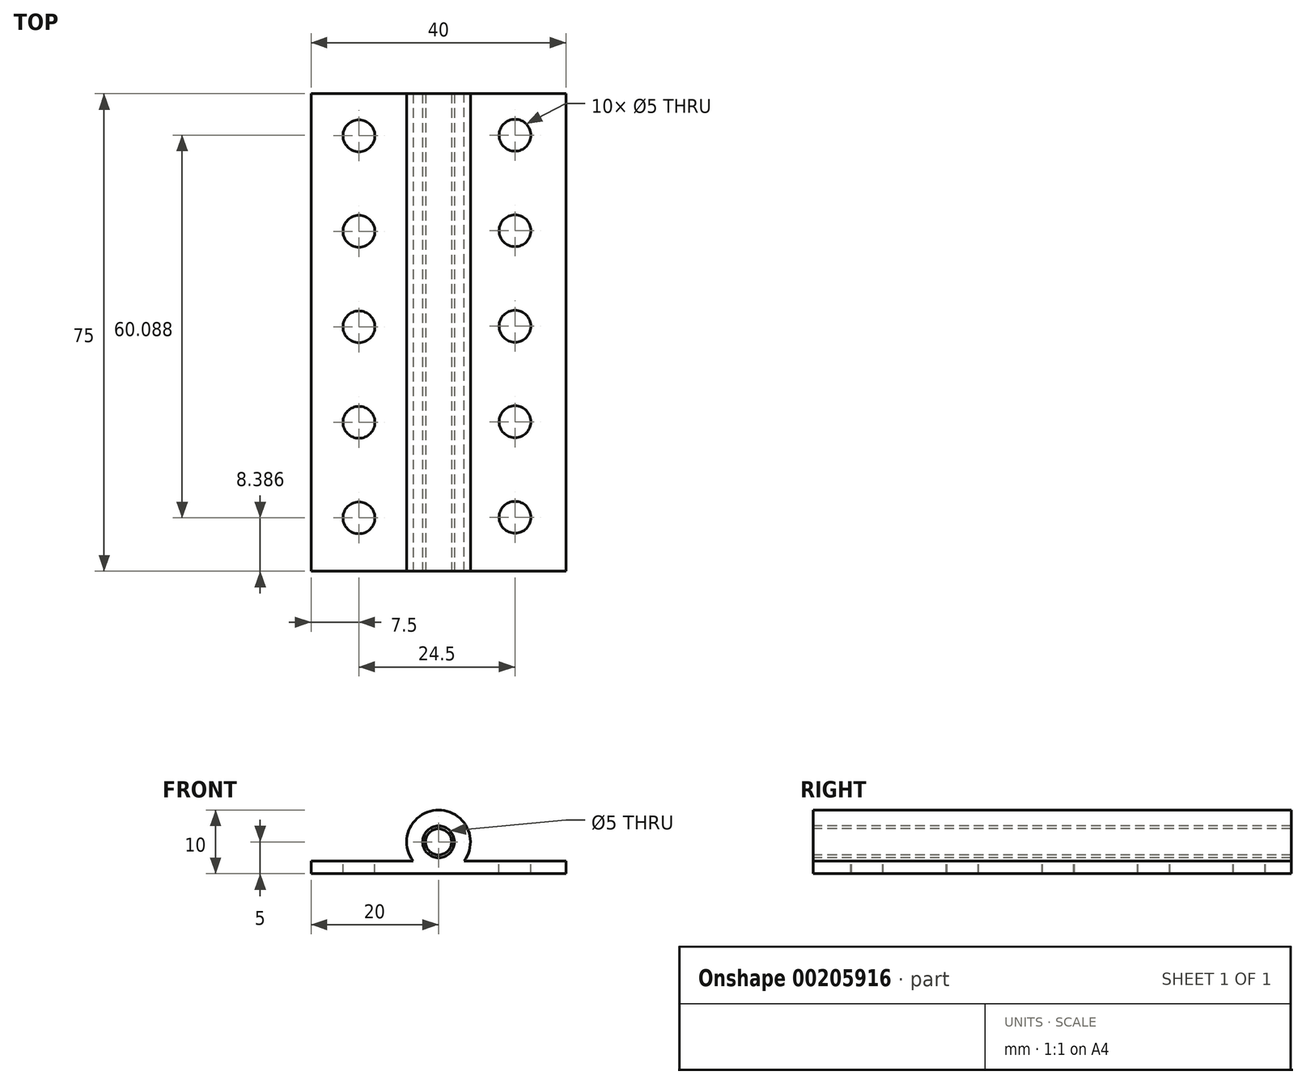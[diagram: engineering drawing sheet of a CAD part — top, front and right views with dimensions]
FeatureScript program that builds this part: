
annotation { "Feature Type Name" : "Feature", "Feature Type Description" : "" }
export const myFeature = defineFeature(function(context is Context, id is Id, definition is map)
    precondition{}
    {
        {
            var Q0;
            Q0=qCreatedBy(makeId("Front.planeOp"),FACE);
            var sketch = newSketch(context, id + "F0", { "sketchPlane" : qUnion([Q0])});
            skCircle(sketch, "E0", {"center": v(0, 0) * mm, "radius": 5 * mm});
            skSolve(sketch);
        }
        {
            var Q0;
            Q0=qCreatedBy(makeId("Front.planeOp"),FACE);
            var sketch = newSketch(context, id + "F1", { "sketchPlane" : qUnion([Q0])});
            skLineSegment(sketch, "E1.bottom", {"start": v(0, -5) * mm, "end": v(20, -5) * mm});
            skLineSegment(sketch, "E1.top", {"start": v(0, -3) * mm, "end": v(20, -3) * mm});
            skLineSegment(sketch, "E1.left", {"start": v(0, -5) * mm, "end": v(0, -3) * mm});
            skLineSegment(sketch, "E1.right", {"start": v(20, -5) * mm, "end": v(20, -3) * mm});
            skSolve(sketch);
        }
        {
            var Q0;
            Q0=makeQuery(id+"F0.imprint","IMPRINT",FACE,{"disambiguationData":[TD([[makeQuery(id+"F0.imprint","IMPRINT",EDGE,{"derivedFrom":sQuery(id+"F0.wireOp",EDGE,"E0")}),1.0]])]});
            var Q1;
            Q1=makeQuery(id+"F1.imprint","IMPRINT",FACE,{"disambiguationData":[TD([[makeQuery(id+"F1.imprint","IMPRINT",EDGE,{"derivedFrom":sQuery(id+"F1.wireOp",EDGE,"E1.bottom")}),1.0]])]});
            extrude(context, id + "F2", {"entities" : qUnion([Q0, Q1]), "depth" : 25 * mm});
        }
        {
            var Q0;
            Q0=makeQuery(id+"F2.opExtrude","CAP_FACE",FACE,{"disambiguationData":[OSD([sQuery(id+"F1.wireOp",EDGE,"E1.bottom"),sQuery(id+"F1.wireOp",EDGE,"E1.top"),sQuery(id+"F1.wireOp",EDGE,"E1.left"),sQuery(id+"F1.wireOp",EDGE,"E1.right")])],"isStart":false});
            extrude(context, id + "F3", {"entities" : qUnion([Q0]), "operationType" : NewBodyOperationType.ADD, "depth" : 25 * mm});
        }
        {
            var Q0;
            Q0=makeQuery(id+"F3.opExtrude","CAP_FACE",FACE,{"disambiguationData":[OSD([sQuery(id+"F1.wireOp",EDGE,"E1.bottom"),sQuery(id+"F1.wireOp",EDGE,"E1.top"),sQuery(id+"F1.wireOp",EDGE,"E1.left"),sQuery(id+"F1.wireOp",EDGE,"E1.right")])],"isStart":false});
            var sketch = newSketch(context, id + "F4", { "sketchPlane" : qUnion([Q0])});
            skCircle(sketch, "E2", {"center": v(0, 0) * mm, "radius": 5 * mm});
            skSolve(sketch);
        }
        {
            var Q0;
            {var subQ1=makeQuery(id+"F3.opExtrude","CAP_EDGE",EDGE,{"disambiguationData":[OSD([sQuery(id+"F1.wireOp",EDGE,"E1.bottom")])],"isStart":false});Q0=makeQuery(id+"F4.imprint","IMPRINT",FACE,{"disambiguationData":[TD([[makeQuery(id+"F4.imprint","IMPRINT",EDGE,{"derivedFrom":subQ1}),1.0]])]});}
            extrude(context, id + "F5", {"entities" : qUnion([Q0]), "operationType" : NewBodyOperationType.ADD, "depth" : 25 * mm});
        }
        {
            var Q0;
            Q0 = qSketchRegion(id + "F4", true);
            extrude(context, id + "F6", {"entities" : qUnion([Q0]), "operationType" : NewBodyOperationType.ADD, "depth" : 25 * mm});
        }
        {
            var Q0;
            {var subQ0=sQuery(id+"F4.wireOp",EDGE,"E2");Q0=makeQuery(id+"F6.boolean.opBoolean","MERGE",FACE,{"derivedFrom":[makeQuery(id+"F5.opExtrude","CAP_FACE",FACE,{"disambiguationData":[OSD([sQuery(id+"F1.wireOp",EDGE,"E1.bottom"),sQuery(id+"F1.wireOp",EDGE,"E1.top"),sQuery(id+"F1.wireOp",EDGE,"E1.right"),subQ0])],"isStart":false}),makeQuery(id+"F6.opExtrude","CAP_FACE",FACE,{"disambiguationData":[OSD([subQ0])],"isStart":false})]});}
            var sketch = newSketch(context, id + "F7", { "sketchPlane" : qUnion([Q0])});
            skCircle(sketch, "E3", {"center": v(0, 0) * mm, "radius": 2.5 * mm});
            skSolve(sketch);
        }
        {
            var Q0;
            Q0=makeQuery(id+"F7.imprint","IMPRINT",FACE,{"disambiguationData":[TD([[makeQuery(id+"F7.imprint","IMPRINT",EDGE,{"derivedFrom":sQuery(id+"F7.wireOp",EDGE,"E3")}),1.0]])]});
            var Q1;
            Q1=sQuery(id+"F7.wireOp",EDGE,"E3");
            extrude(context, id + "F8", {"entities" : qUnion([Q0]), "operationType" : NewBodyOperationType.REMOVE, "surfaceEntities" : qUnion([Q1]), "oppositeDirection" : true, "depth" : 85.7 * mm});
        }
        {
            var Q0;
            Q0=makeQuery(id+"F2.opExtrude","CAP_FACE",FACE,{"disambiguationData":[OSD([sQuery(id+"F0.wireOp",EDGE,"E0")])],"isStart":false});
            extrude(context, id + "F9", {"entities" : qUnion([Q0]), "operationType" : NewBodyOperationType.REMOVE, "depth" : 25 * mm});
        }
        {
            var Q0;
            Q0=makeQuery(id+"F2.opExtrude","CAP_FACE",FACE,{"disambiguationData":[OSD([sQuery(id+"F0.wireOp",EDGE,"E0")])],"isStart":false});
            var sketch = newSketch(context, id + "F10", { "sketchPlane" : qUnion([Q0])});
            skCircle(sketch, "E4", {"center": v(0, 0) * mm, "radius": 5 * mm});
            skSolve(sketch);
        }
        {
            var Q0;
            Q0 = qSketchRegion(id + "F10", true);
            extrude(context, id + "F11", {"entities" : qUnion([Q0]), "operationType" : NewBodyOperationType.REMOVE, "depth" : 25 * mm});
        }
        {
            var Q0;
            {var subQ0=sQuery(id+"F1.wireOp",EDGE,"E1.top");Q0=makeQuery(id+"F5.boolean.opBoolean","MERGE",FACE,{"derivedFrom":[makeQuery(id+"F3.boolean.opBoolean","MERGE",FACE,{"derivedFrom":[makeQuery(id+"F2.opExtrude","SWEPT_FACE",FACE,{"disambiguationData":[OSD([subQ0])]}),makeQuery(id+"F3.opExtrude","SWEPT_FACE",FACE,{"disambiguationData":[OSD([subQ0])]})]}),makeQuery(id+"F5.opExtrude","SWEPT_FACE",FACE,{"disambiguationData":[OSD([subQ0])]})]});}
            var sketch = newSketch(context, id + "F12", { "sketchPlane" : qUnion([Q0])});
            skCircle(sketch, "E5", {"center": v(12, -6.53) * mm, "radius": 2.5 * mm});
            skCircle(sketch, "E6", {"center": v(12, -21.53) * mm, "radius": 2.5 * mm});
            skCircle(sketch, "E7", {"center": v(12, -36.53) * mm, "radius": 2.5 * mm});
            skCircle(sketch, "E8", {"center": v(12, -51.53) * mm, "radius": 2.5 * mm});
            skCircle(sketch, "E9", {"center": v(12, -66.53) * mm, "radius": 2.5 * mm});
            skSolve(sketch);
        }
        {
            var Q0;
            Q0=makeQuery(id+"F12.imprint","IMPRINT",FACE,{"disambiguationData":[TD([[makeQuery(id+"F12.imprint","IMPRINT",EDGE,{"derivedFrom":sQuery(id+"F12.wireOp",EDGE,"E5")}),1.0]])]});
            var Q1;
            Q1=makeQuery(id+"F12.imprint","IMPRINT",FACE,{"disambiguationData":[TD([[makeQuery(id+"F12.imprint","IMPRINT",EDGE,{"derivedFrom":sQuery(id+"F12.wireOp",EDGE,"E6")}),1.0]])]});
            var Q2;
            Q2=makeQuery(id+"F12.imprint","IMPRINT",FACE,{"disambiguationData":[TD([[makeQuery(id+"F12.imprint","IMPRINT",EDGE,{"derivedFrom":sQuery(id+"F12.wireOp",EDGE,"E7")}),1.0]])]});
            var Q3;
            Q3=makeQuery(id+"F12.imprint","IMPRINT",FACE,{"disambiguationData":[TD([[makeQuery(id+"F12.imprint","IMPRINT",EDGE,{"derivedFrom":sQuery(id+"F12.wireOp",EDGE,"E8")}),1.0]])]});
            var Q4;
            Q4=makeQuery(id+"F12.imprint","IMPRINT",FACE,{"disambiguationData":[TD([[makeQuery(id+"F12.imprint","IMPRINT",EDGE,{"derivedFrom":sQuery(id+"F12.wireOp",EDGE,"E9")}),1.0]])]});
            var Q5;
            Q5=sQuery(id+"F12.wireOp",EDGE,"E5");
            var Q6;
            Q6=sQuery(id+"F12.wireOp",EDGE,"E6");
            var Q7;
            Q7=sQuery(id+"F12.wireOp",EDGE,"E7");
            var Q8;
            Q8=sQuery(id+"F12.wireOp",EDGE,"E8");
            var Q9;
            Q9=sQuery(id+"F12.wireOp",EDGE,"E9");
            extrude(context, id + "F13", {"entities" : qUnion([Q0, Q1, Q2, Q3, Q4]), "operationType" : NewBodyOperationType.REMOVE, "surfaceEntities" : qUnion([Q5, Q6, Q7, Q8, Q9]), "oppositeDirection" : true, "depth" : 25 * mm});
        }
        {
            var Q0;
            {var subQ0=sQuery(id+"F4.wireOp",EDGE,"E2");Q0=makeQuery(id+"F6.boolean.opBoolean","MERGE",FACE,{"derivedFrom":[makeQuery(id+"F5.opExtrude","CAP_FACE",FACE,{"disambiguationData":[OSD([sQuery(id+"F1.wireOp",EDGE,"E1.bottom"),sQuery(id+"F1.wireOp",EDGE,"E1.top"),sQuery(id+"F1.wireOp",EDGE,"E1.right"),subQ0])],"isStart":false}),makeQuery(id+"F6.opExtrude","CAP_FACE",FACE,{"disambiguationData":[OSD([subQ0])],"isStart":false})]});}
            var sketch = newSketch(context, id + "F14", { "sketchPlane" : qUnion([Q0])});
            skLineSegment(sketch, "E10.bottom", {"start": v(0, -5) * mm, "end": v(-20, -5) * mm});
            skLineSegment(sketch, "E10.top", {"start": v(0, -3) * mm, "end": v(-20, -3) * mm});
            skLineSegment(sketch, "E10.left", {"start": v(0, -5) * mm, "end": v(0, -3) * mm});
            skLineSegment(sketch, "E10.right", {"start": v(-20, -5) * mm, "end": v(-20, -3) * mm});
            skSolve(sketch);
        }
        {
            var Q0;
            {var subQ0=sQuery(id+"F14.wireOp",EDGE,"E10.bottom");Q0=makeQuery(id+"F14.imprint","IMPRINT",FACE,{"disambiguationData":[TD([[makeQuery(id+"F14.imprint","IMPRINT",EDGE,{"derivedFrom":subQ0}),-1.0]])]});}
            extrude(context, id + "F15", {"entities" : qUnion([Q0]), "oppositeDirection" : true, "depth" : 75 * mm});
        }
        {
            var Q0;
            Q0=makeQuery(id+"F11.boolean.opBoolean","MERGE",FACE,{"derivedFrom":[makeQuery(id+"F2.opExtrude","CAP_FACE",FACE,{"disambiguationData":[OSD([sQuery(id+"F0.wireOp",EDGE,"E0")])],"isStart":false}),makeQuery(id+"F11.opExtrude","CAP_FACE",FACE,{"disambiguationData":[OSD([sQuery(id+"F10.wireOp",EDGE,"E4")])],"isStart":true})]});
            extrude(context, id + "F16", {"entities" : qUnion([Q0]), "operationType" : NewBodyOperationType.ADD, "depth" : 25 * mm});
        }
        {
            var Q0;
            {var subQ0=sQuery(id+"F4.wireOp",EDGE,"E2");Q0=makeQuery(id+"F6.boolean.opBoolean","MERGE",FACE,{"derivedFrom":[makeQuery(id+"F5.opExtrude","CAP_FACE",FACE,{"disambiguationData":[OSD([sQuery(id+"F1.wireOp",EDGE,"E1.bottom"),sQuery(id+"F1.wireOp",EDGE,"E1.top"),sQuery(id+"F1.wireOp",EDGE,"E1.right"),subQ0])],"isStart":false}),makeQuery(id+"F6.opExtrude","CAP_FACE",FACE,{"disambiguationData":[OSD([subQ0])],"isStart":false})]});}
            var sketch = newSketch(context, id + "F17", { "sketchPlane" : qUnion([Q0])});
            skCircle(sketch, "E11", {"center": v(0, 0) * mm, "radius": 2.05 * mm});
            skSolve(sketch);
        }
        {
            var Q0;
            Q0=makeQuery(id+"F17.imprint","IMPRINT",FACE,{"disambiguationData":[TD([[makeQuery(id+"F17.imprint","IMPRINT",EDGE,{"derivedFrom":sQuery(id+"F17.wireOp",EDGE,"E11")}),1.0]])]});
            extrude(context, id + "F18", {"entities" : qUnion([Q0]), "oppositeDirection" : true, "depth" : 75 * mm});
        }
        {
            var Q0;
            Q0=makeQuery(id+"F15.opExtrude","SWEPT_FACE",FACE,{"disambiguationData":[OSD([sQuery(id+"F14.wireOp",EDGE,"E10.top")])]});
            var sketch = newSketch(context, id + "F19", { "sketchPlane" : qUnion([Q0])});
            skCircle(sketch, "E12", {"center": v(-12.5, -6.61) * mm, "radius": 2.5 * mm});
            skCircle(sketch, "E13", {"center": v(-12.5, -21.61) * mm, "radius": 2.5 * mm});
            skCircle(sketch, "E14", {"center": v(-12.5, -36.61) * mm, "radius": 2.5 * mm});
            skCircle(sketch, "E15", {"center": v(-12.5, -51.61) * mm, "radius": 2.5 * mm});
            skCircle(sketch, "E16", {"center": v(-12.5, -66.61) * mm, "radius": 2.5 * mm});
            skSolve(sketch);
        }
        {
            var Q0;
            Q0=makeQuery(id+"F19.imprint","IMPRINT",FACE,{"disambiguationData":[TD([[makeQuery(id+"F19.imprint","IMPRINT",EDGE,{"derivedFrom":sQuery(id+"F19.wireOp",EDGE,"E12")}),1.0]])]});
            var Q1;
            Q1=makeQuery(id+"F19.imprint","IMPRINT",FACE,{"disambiguationData":[TD([[makeQuery(id+"F19.imprint","IMPRINT",EDGE,{"derivedFrom":sQuery(id+"F19.wireOp",EDGE,"E13")}),1.0]])]});
            var Q2;
            Q2=makeQuery(id+"F19.imprint","IMPRINT",FACE,{"disambiguationData":[TD([[makeQuery(id+"F19.imprint","IMPRINT",EDGE,{"derivedFrom":sQuery(id+"F19.wireOp",EDGE,"E14")}),1.0]])]});
            var Q3;
            Q3=makeQuery(id+"F19.imprint","IMPRINT",FACE,{"disambiguationData":[TD([[makeQuery(id+"F19.imprint","IMPRINT",EDGE,{"derivedFrom":sQuery(id+"F19.wireOp",EDGE,"E15")}),1.0]])]});
            var Q4;
            Q4=makeQuery(id+"F19.imprint","IMPRINT",FACE,{"disambiguationData":[TD([[makeQuery(id+"F19.imprint","IMPRINT",EDGE,{"derivedFrom":sQuery(id+"F19.wireOp",EDGE,"E16")}),1.0]])]});
            extrude(context, id + "F20", {"entities" : qUnion([Q0, Q1, Q2, Q3, Q4]), "operationType" : NewBodyOperationType.REMOVE, "oppositeDirection" : true, "depth" : 25 * mm});
        }
    });
